# Revit family: DoorOperator_OverheadDoor_RMX
name_source: partatom
category: Generic Models
units: mm (PartAtom-declared; Revit-internal decimal feet)

## family parameters
Always vertical = No
Can host rebar = No
Classification Number = 23.30.40.11.34
Cut with Voids When Loaded = No
Maintain Annotation Orientation = No
Part Type = Normal
Room Calculation Point = No
Round Connector Dimension = Use Diameter
Shared = No
Work Plane-Based = Yes

## types (36) — shared parameters
Assembly Code = B2030410
Construction Details = https://www.arcat.com
Default Elevation = 4' - 0"
Description = Overhead Door Corporation Overhead Door Operator Model RMX
Green Building-LEED = https://www.arcat.com
Keynote = 08 71 13
Manufacturer = Overhead Door Corporation
Model = RMX
Product Data = http://www.arcat.com
SpecWizard = https://www.arcat.com
Specification = https://www.arcat.com
URL = http://www.overheaddoor.com

## type names (no varying parameters)
- Rolling Steel Door - 671 - 1/2HP
- Rolling Steel Door - 670 - 1/2HP
- Rolling Steel Door - 650/651/652 - 1/2HP
- Rolling Steel Door - 640/641 - 1/2HP
- Rolling Steel Door - 630/631/634 18ga - 1/2HP
- Rolling Steel Door - 630/631/634 20ga - 1/2HP
- Rolling Steel Door - 630/631/634 22ga - 1/2HP
- Rolling Steel Door - 630/631/634 24ga - 1/2HP
- Rolling Steel Door - 635 22ga - 1/2HP
- Rolling Steel Door - 635 24ga - 1/2HP
- Rolling Steel Door - 625 18ga - 1/2HP
- Rolling Steel Door - 625 20ga - 1/2HP
- Rolling Steel Door - 625 22ga - 1/2HP
- Rolling Steel Door - 625 24ga - 1/2HP
- Rolling Steel Door - 610/620 18ga - 1/2HP
- Rolling Steel Door - 610/620 20ga - 1/2HP
- Rolling Steel Door - 610/620 22ga - 1/2HP
- Rolling Steel Door - 610 - 1/2HP
- Rolling Steel Door - 600 - 1/2HP
- Sectional Door - 521 - 1/2HP
- Sectional Door - 511 - 1/2HP
- Sectional Door - 599 - 1/2HP
- Sectional Door - 598 - 1/2HP
- Sectional Door - 596 - 1/2HP
- Sectional Door - 594 - 1/2HP
- Sectional Door - 593 - 1/2HP
- Sectional Door - 592 - 1/2HP
- Sectional Door - 591 - 1/2HP
- Sectional Door - 432 - 1/2HP
- Sectional Door - 430 - 1/2HP
- Sectional Door - 426 - 1/2HP
- Sectional Door - 424 - 1/2HP
- Sectional Door - 422 - 1/2HP
- Sectional Door - 420 - 1/2HP
- Sectional Door - 418 - 1/2HP
- Sectional Door - 160 - 1/2HP

## geometry (parser evidence)
native form markers: Blend x4, Sweep x5
no freeform markers — native parametric forms only
